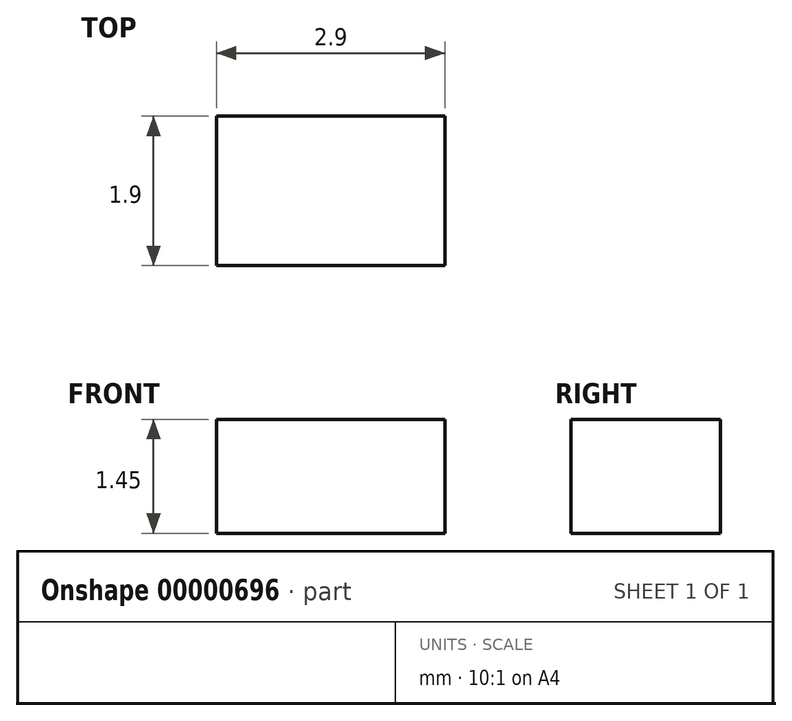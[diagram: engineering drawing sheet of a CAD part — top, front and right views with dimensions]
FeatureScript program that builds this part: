
annotation { "Feature Type Name" : "Feature", "Feature Type Description" : "" }
export const myFeature = defineFeature(function(context is Context, id is Id, definition is map)
    precondition{}
    {
        {
            var Q0;
            Q0=qCreatedBy(makeId("Top.planeOp"),FACE);
            var sketch = newSketch(context, id + "F0", { "sketchPlane" : qUnion([Q0])});
            skLineSegment(sketch, "E0.bottom", {"start": v(0, 0) * mm, "end": v(2.9, 0) * mm});
            skLineSegment(sketch, "E0.top", {"start": v(0, 1.9) * mm, "end": v(2.9, 1.9) * mm});
            skLineSegment(sketch, "E0.left", {"start": v(0, 0) * mm, "end": v(0, 1.9) * mm});
            skLineSegment(sketch, "E0.right", {"start": v(2.9, 0) * mm, "end": v(2.9, 1.9) * mm});
            skSolve(sketch);
        }
        {
            var Q0;
            Q0=makeQuery(id+"F0.imprint","IMPRINT",FACE,{"disambiguationData":[TD([[makeQuery(id+"F0.imprint","IMPRINT",EDGE,{"derivedFrom":sQuery(id+"F0.wireOp",EDGE,"E0.bottom")}),1.0]])]});
            extrude(context, id + "F1", {"entities" : qUnion([Q0]), "depth" : 1.45 * mm});
        }
    });
